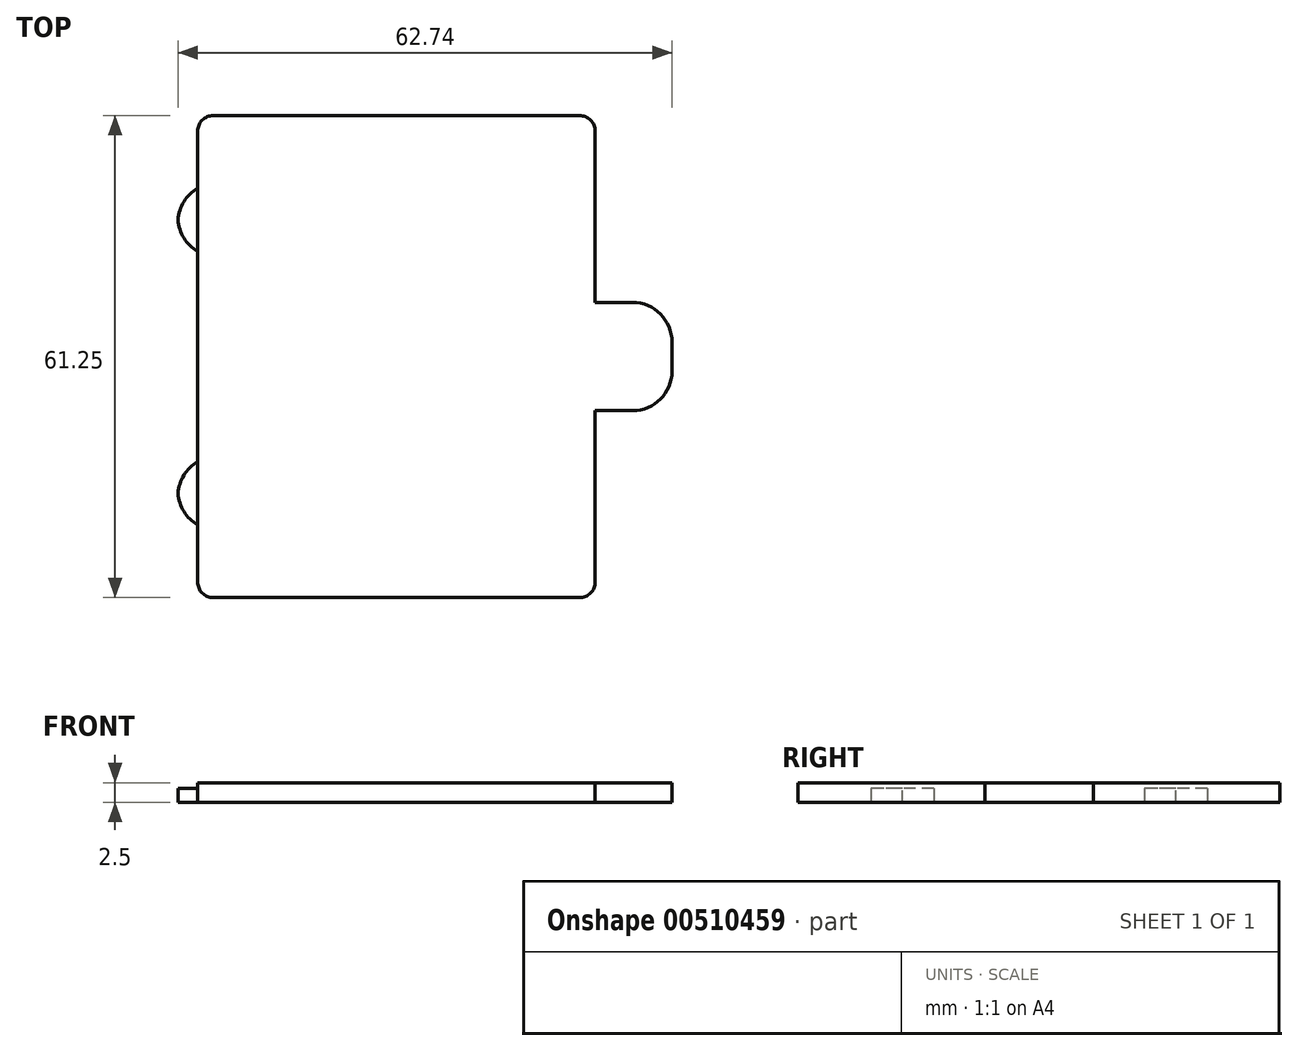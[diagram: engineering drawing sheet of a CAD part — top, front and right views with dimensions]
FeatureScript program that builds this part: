
annotation { "Feature Type Name" : "Feature", "Feature Type Description" : "" }
export const myFeature = defineFeature(function(context is Context, id is Id, definition is map)
    precondition{}
    {
        {
            var Q0;
            Q0=qCreatedBy(makeId("Top.planeOp"),FACE);
            var sketch = newSketch(context, id + "F0", { "sketchPlane" : qUnion([Q0])});
            skLineSegment(sketch, "E0.bottom", {"start": v(-25.4, 39.34) * mm, "end": v(25.1, 39.34) * mm});
            skLineSegment(sketch, "E0.top", {"start": v(-25.4, -21.91) * mm, "end": v(25.1, -21.91) * mm});
            skLineSegment(sketch, "E0.left", {"start": v(-25.4, 39.34) * mm, "end": v(-25.4, -21.91) * mm});
            skLineSegment(sketch, "E0.right", {"start": v(25.1, 39.34) * mm, "end": v(25.1, -21.91) * mm});
            skLineSegment(sketch, "E1.bottom", {"start": v(25.1, 15.59) * mm, "end": v(34.85, 15.59) * mm});
            skLineSegment(sketch, "E1.top", {"start": v(25.1, 1.84) * mm, "end": v(34.85, 1.84) * mm});
            skLineSegment(sketch, "E1.left", {"start": v(25.1, 15.59) * mm, "end": v(25.1, 1.84) * mm});
            skLineSegment(sketch, "E1.right", {"start": v(34.85, 15.59) * mm, "end": v(34.85, 1.84) * mm});
            skLineSegment(sketch, "E2.bottom", {"start": v(-25.4, 30.09) * mm, "end": v(-27.9, 30.09) * mm});
            skLineSegment(sketch, "E2.top", {"start": v(-25.4, 22.09) * mm, "end": v(-27.9, 22.09) * mm});
            skLineSegment(sketch, "E2.left", {"start": v(-25.4, 30.09) * mm, "end": v(-25.4, 22.09) * mm});
            skLineSegment(sketch, "E2.right", {"start": v(-27.9, 30.09) * mm, "end": v(-27.9, 22.09) * mm});
            skLineSegment(sketch, "E3.bottom", {"start": v(-25.4, -4.66) * mm, "end": v(-27.9, -4.66) * mm});
            skLineSegment(sketch, "E3.top", {"start": v(-25.4, -12.66) * mm, "end": v(-27.9, -12.66) * mm});
            skLineSegment(sketch, "E3.left", {"start": v(-25.4, -4.66) * mm, "end": v(-25.4, -12.66) * mm});
            skLineSegment(sketch, "E3.right", {"start": v(-27.9, -4.66) * mm, "end": v(-27.9, -12.66) * mm});
            skSolve(sketch);
        }
        {
            var Q0;
            {var subQ3=sQuery(id+"F0.wireOp",EDGE,"E0.bottom");Q0=makeQuery(id+"F0.imprint","IMPRINT",FACE,{"disambiguationData":[TD([[makeQuery(id+"F0.imprint","IMPRINT",EDGE,{"derivedFrom":subQ3}),-1.0]])]});}
            var Q1;
            Q1=makeQuery(id+"F0.imprint","IMPRINT",FACE,{"disambiguationData":[TD([[makeQuery(id+"F0.imprint","IMPRINT",EDGE,{"derivedFrom":sQuery(id+"F0.wireOp",EDGE,"E1.bottom")}),-1.0]])]});
            extrude(context, id + "F1", {"entities" : qUnion([Q0, Q1]), "depth" : 2.5 * mm});
        }
        {
            var Q0;
            Q0=makeQuery(id+"F0.imprint","IMPRINT",FACE,{"disambiguationData":[TD([[makeQuery(id+"F0.imprint","IMPRINT",EDGE,{"derivedFrom":sQuery(id+"F0.wireOp",EDGE,"E2.bottom")}),1.0]])]});
            var Q1;
            Q1=makeQuery(id+"F0.imprint","IMPRINT",FACE,{"disambiguationData":[TD([[makeQuery(id+"F0.imprint","IMPRINT",EDGE,{"derivedFrom":sQuery(id+"F0.wireOp",EDGE,"E3.bottom")}),1.0]])]});
            extrude(context, id + "F2", {"entities" : qUnion([Q0, Q1]), "operationType" : NewBodyOperationType.ADD, "depth" : 1.75 * mm});
        }
        {
            var Q0;
            Q0=makeQuery(id+"F1.opExtrude","SWEPT_EDGE",EDGE,{"disambiguationData":[OSD([sQuery(id+"F0.wireOp",EDGE,"E0.bottom"),sQuery(id+"F0.wireOp",EDGE,"E0.left")])]});
            var Q1;
            Q1=makeQuery(id+"F1.opExtrude","SWEPT_EDGE",EDGE,{"disambiguationData":[OSD([sQuery(id+"F0.wireOp",EDGE,"E0.top"),sQuery(id+"F0.wireOp",EDGE,"E0.left")])]});
            var Q2;
            Q2=makeQuery(id+"F1.opExtrude","SWEPT_EDGE",EDGE,{"disambiguationData":[OSD([sQuery(id+"F0.wireOp",EDGE,"E0.top"),sQuery(id+"F0.wireOp",EDGE,"E0.right")])]});
            var Q3;
            Q3=makeQuery(id+"F1.opExtrude","SWEPT_EDGE",EDGE,{"disambiguationData":[OSD([sQuery(id+"F0.wireOp",EDGE,"E0.bottom"),sQuery(id+"F0.wireOp",EDGE,"E0.right")])]});
            fillet(context, id + "F3", {"entities" : qUnion([Q0, Q1, Q2, Q3]), "radius" : 2 * mm, "tangentPropagation" : true, "allowEdgeOverflow" : false});
        }
        {
            var Q0;
            Q0=makeQuery(id+"F1.opExtrude","SWEPT_EDGE",EDGE,{"disambiguationData":[OSD([sQuery(id+"F0.wireOp",EDGE,"E1.top"),sQuery(id+"F0.wireOp",EDGE,"E1.right")])]});
            var Q1;
            Q1=makeQuery(id+"F1.opExtrude","SWEPT_EDGE",EDGE,{"disambiguationData":[OSD([sQuery(id+"F0.wireOp",EDGE,"E1.bottom"),sQuery(id+"F0.wireOp",EDGE,"E1.right")])]});
            fillet(context, id + "F4", {"entities" : qUnion([Q0, Q1]), "radius" : 5 * mm, "tangentPropagation" : true, "allowEdgeOverflow" : false});
        }
        {
            var Q0;
            Q0=makeQuery(id+"F2.opExtrude","SWEPT_EDGE",EDGE,{"disambiguationData":[OSD([sQuery(id+"F0.wireOp",EDGE,"E2.bottom"),sQuery(id+"F0.wireOp",EDGE,"E2.right")])]});
            var Q1;
            Q1=makeQuery(id+"F2.opExtrude","SWEPT_EDGE",EDGE,{"disambiguationData":[OSD([sQuery(id+"F0.wireOp",EDGE,"E2.top"),sQuery(id+"F0.wireOp",EDGE,"E2.right")])]});
            var Q2;
            Q2=makeQuery(id+"F2.opExtrude","SWEPT_EDGE",EDGE,{"disambiguationData":[OSD([sQuery(id+"F0.wireOp",EDGE,"E3.bottom"),sQuery(id+"F0.wireOp",EDGE,"E3.right")])]});
            var Q3;
            Q3=makeQuery(id+"F2.opExtrude","SWEPT_EDGE",EDGE,{"disambiguationData":[OSD([sQuery(id+"F0.wireOp",EDGE,"E3.top"),sQuery(id+"F0.wireOp",EDGE,"E3.right")])]});
            fillet(context, id + "F5", {"entities" : qUnion([Q0, Q1, Q2, Q3]), "radius" : 5 * mm, "tangentPropagation" : true, "allowEdgeOverflow" : false});
        }
    });
